# Revit family: 306_b223ac7f6b9e48b0bcc7016f55d9b9
name_source: partatom
category: Pipe Accessories
units: mm (PartAtom-declared; Revit-internal decimal feet)

## family parameters
Always vertical = Yes
Cut with Voids When Loaded = No
Part Type = Valve - Breaks Into
Round Connector Dimension = Use Diameter
Shared = No
Work Plane-Based = No

## types (6) — shared parameters
Description = Pressure reducing valve, nominal pressure 25 bar, M-M conn.
L22 = 2 mm  [stored 0.00656168 ft]
L2D = 150 mm
L2D_Min = 3048 mm
LL = 3 mm  [stored 0.00984252 ft]
LLL = 6 mm  [stored 0.019685 ft]
LL__ve = -3 mm  [stored -0.00984252 ft]
Manufacturer = FAR
QmdConnectorList = 301;D;302;D
R52 = 8 mm  [stored 0.0262467 ft]
W2D = 25 mm  [stored 0.082021 ft]
magiPartTypeId = 306
magiProductFamilyId = b223ac7f6b9e48b0bcc7016f55d9b9
zero-valued in all types: Default Elevation

## per-type parameters (varying)
- 2800 1: CenSd_R2_6=13 mm  [stored 0.0426509 ft]; CenSd_R32_6=19 mm  [stored 0.062336 ft]; CenSd_R3_6=18 mm  [stored 0.0590551 ft]; D=25 mm; H=157 mm; H10=14 mm  [stored 0.0459318 ft]; H3=39 mm; H5=26 mm  [stored 0.0853018 ft]; HH2=17 mm  [stored 0.0557743 ft]; L2=75 mm; LH=60 mm; NT=15 mm  [stored 0.0492126 ft]; NT2=30 mm  [stored 0.0984252 ft]; NT__ve=-15 mm  [stored -0.0492126 ft]; R=13 mm  [stored 0.0426509 ft]; R1=17 mm  [stored 0.0557743 ft]; R2=15 mm  [stored 0.0492126 ft]; R24=19 mm  [stored 0.062336 ft]; R25=17 mm  [stored 0.0557743 ft]; R3=21 mm; R32=22 mm; R5=32 mm  [stored 0.104987 ft]; R6=34 mm  [stored 0.111549 ft]; TLL=15 mm  [stored 0.0492126 ft]; TLL__ve=-15 mm  [stored -0.0492126 ft]; magiProductId=25152e4836604e1d8fbe4be3ce001b
- 2800 112: CenSd_R2_6=19 mm  [stored 0.062336 ft]; CenSd_R32_6=25 mm  [stored 0.082021 ft]; CenSd_R3_6=24 mm  [stored 0.0787402 ft]; D=40 mm; H=162 mm; H10=15 mm  [stored 0.0492126 ft]; H3=41 mm; H5=27 mm  [stored 0.0885827 ft]; HH2=24 mm  [stored 0.0787402 ft]; L2=88 mm; LH=62 mm; NT=18 mm  [stored 0.0590551 ft]; NT2=35 mm  [stored 0.114829 ft]; NT__ve=-18 mm  [stored -0.0590551 ft]; R=20 mm  [stored 0.0656168 ft]; R1=24 mm  [stored 0.0787402 ft]; R2=23 mm; R24=27 mm  [stored 0.0885827 ft]; R25=25 mm  [stored 0.082021 ft]; R3=28 mm  [stored 0.0918635 ft]; R32=29 mm  [stored 0.0951444 ft]; R5=38 mm; R6=40 mm; TLL=18 mm  [stored 0.0590551 ft]; TLL__ve=-18 mm  [stored -0.0590551 ft]; magiProductId=c08a6f1942e74f81b70147ea77004e
- 2800 114: CenSd_R2_6=16 mm  [stored 0.0524934 ft]; CenSd_R32_6=22 mm; CenSd_R3_6=21 mm; D=32 mm; H=161 mm; H10=15 mm  [stored 0.0492126 ft]; H3=40 mm; H5=27 mm  [stored 0.0885827 ft]; HH2=20 mm  [stored 0.0656168 ft]; L2=80 mm; LH=62 mm; NT=16 mm  [stored 0.0524934 ft]; NT2=32 mm  [stored 0.104987 ft]; NT__ve=-16 mm  [stored -0.0524934 ft]; R=16 mm  [stored 0.0524934 ft]; R1=20 mm  [stored 0.0656168 ft]; R2=19 mm  [stored 0.062336 ft]; R24=23 mm; R25=21 mm; R3=24 mm  [stored 0.0787402 ft]; R32=25 mm  [stored 0.082021 ft]; R5=34 mm  [stored 0.111549 ft]; R6=36 mm  [stored 0.11811 ft]; TLL=16 mm  [stored 0.0524934 ft]; TLL__ve=-16 mm  [stored -0.0524934 ft]; magiProductId=5a0a3ccc04384ee8b18895e05ba843
- 2800 12: CenSd_R2_6=9 mm; CenSd_R32_6=14 mm  [stored 0.0459318 ft]; CenSd_R3_6=13 mm  [stored 0.0426509 ft]; D=15 mm; H=121 mm; H10=11 mm  [stored 0.0360892 ft]; H3=30 mm  [stored 0.0984252 ft]; H5=20 mm  [stored 0.0656168 ft]; HH2=12 mm  [stored 0.0393701 ft]; L2=61 mm; LH=46 mm; NT=12 mm  [stored 0.0393701 ft]; NT2=24 mm  [stored 0.0787402 ft]; NT__ve=-12 mm  [stored -0.0393701 ft]; R=8 mm  [stored 0.0262467 ft]; R1=12 mm  [stored 0.0393701 ft]; R2=10 mm  [stored 0.0328084 ft]; R24=14 mm  [stored 0.0459318 ft]; R25=12 mm  [stored 0.0393701 ft]; R3=16 mm  [stored 0.0524934 ft]; R32=17 mm  [stored 0.0557743 ft]; R5=25 mm  [stored 0.082021 ft]; R6=27 mm  [stored 0.0885827 ft]; TLL=12 mm  [stored 0.0393701 ft]; TLL__ve=-12 mm  [stored -0.0393701 ft]; magiProductId=6a712f76ac7c4cfa81f5735f466b94
- 2800 2: CenSd_R2_6=24 mm  [stored 0.0787402 ft]; CenSd_R32_6=29 mm  [stored 0.0951444 ft]; CenSd_R3_6=29 mm  [stored 0.0951444 ft]; D=50 mm; H=162 mm; H10=15 mm  [stored 0.0492126 ft]; H3=41 mm; H5=27 mm  [stored 0.0885827 ft]; HH2=29 mm  [stored 0.0951444 ft]; L2=95 mm; LH=62 mm; NT=19 mm  [stored 0.062336 ft]; NT2=38 mm; NT__ve=-19 mm  [stored -0.062336 ft]; R=25 mm  [stored 0.082021 ft]; R1=29 mm  [stored 0.0951444 ft]; R2=28 mm  [stored 0.0918635 ft]; R24=32 mm  [stored 0.104987 ft]; R25=30 mm  [stored 0.0984252 ft]; R3=33 mm  [stored 0.108268 ft]; R32=34 mm  [stored 0.111549 ft]; R5=42 mm; R6=44 mm; TLL=20 mm  [stored 0.0656168 ft]; TLL__ve=-20 mm  [stored -0.0656168 ft]; magiProductId=8139b10aeeab483ebb5c552e93f462
- 2800 34: CenSd_R2_6=11 mm  [stored 0.0360892 ft]; CenSd_R32_6=16 mm  [stored 0.0524934 ft]; CenSd_R3_6=16 mm  [stored 0.0524934 ft]; D=20 mm; H=121 mm; H10=11 mm  [stored 0.0360892 ft]; H3=30 mm  [stored 0.0984252 ft]; H5=20 mm  [stored 0.0656168 ft]; HH2=14 mm  [stored 0.0459318 ft]; L2=65 mm; LH=46 mm; NT=13 mm  [stored 0.0426509 ft]; NT2=26 mm  [stored 0.0853018 ft]; NT__ve=-13 mm  [stored -0.0426509 ft]; R=10 mm  [stored 0.0328084 ft]; R1=14 mm  [stored 0.0459318 ft]; R2=13 mm  [stored 0.0426509 ft]; R24=17 mm  [stored 0.0557743 ft]; R25=15 mm  [stored 0.0492126 ft]; R3=18 mm  [stored 0.0590551 ft]; R32=19 mm  [stored 0.062336 ft]; R5=27 mm  [stored 0.0885827 ft]; R6=29 mm  [stored 0.0951444 ft]; TLL=13 mm  [stored 0.0426509 ft]; TLL__ve=-13 mm  [stored -0.0426509 ft]; magiProductId=8636823e8e654d7caf5087061e43f8

note: column(s) folded — value = type name in every type: MC Product Code

note: [stored X ft] marks values corroborated as IEEE doubles in the binary element streams (Revit-internal decimal feet)

## geometry (parser evidence)
native form markers: Sweep x1
no freeform markers — native parametric forms only
